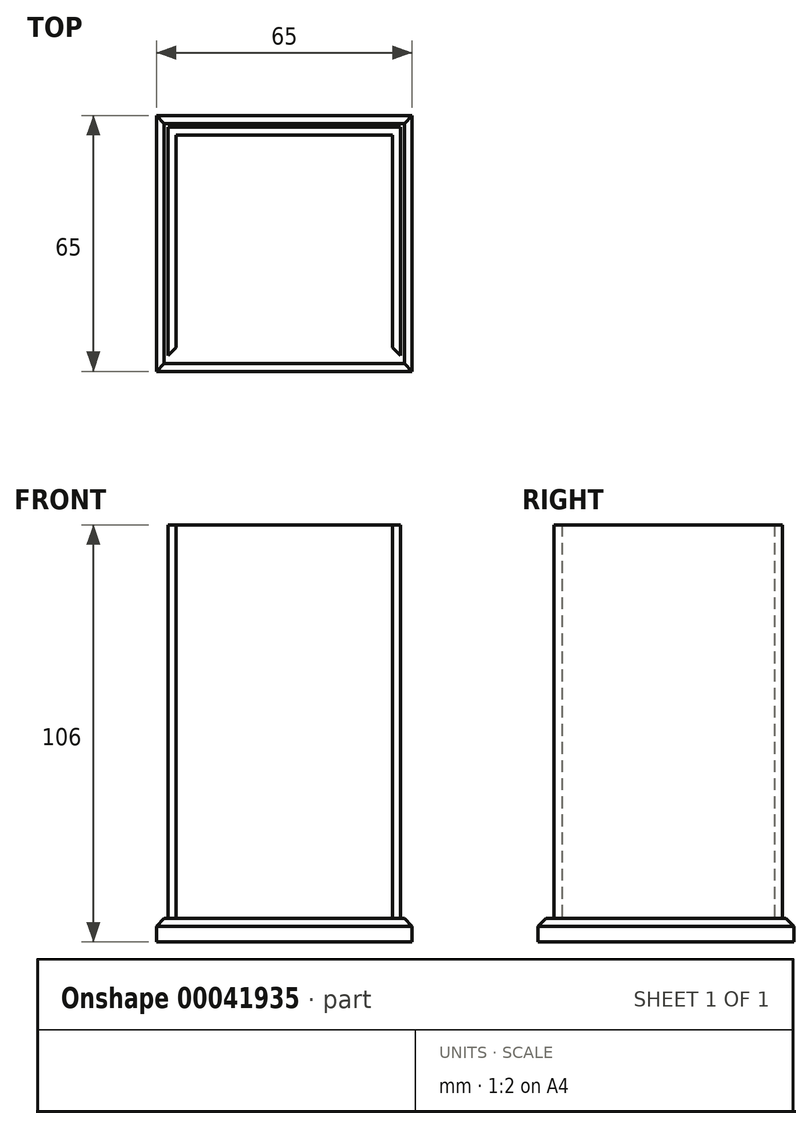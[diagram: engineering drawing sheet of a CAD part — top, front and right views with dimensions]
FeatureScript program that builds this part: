
annotation { "Feature Type Name" : "Feature", "Feature Type Description" : "" }
export const myFeature = defineFeature(function(context is Context, id is Id, definition is map)
    precondition{}
    {
        {
            var Q0;
            Q0=qCreatedBy(makeId("Top.planeOp"),FACE);
            var sketch = newSketch(context, id + "F0", { "sketchPlane" : qUnion([Q0])});
            skLineSegment(sketch, "E0.rect.bottom", {"start": v(32.5, -32.5) * mm, "end": v(-32.5, -32.5) * mm});
            skLineSegment(sketch, "E0.rect.top", {"start": v(32.5, 32.5) * mm, "end": v(-32.5, 32.5) * mm});
            skLineSegment(sketch, "E0.rect.left", {"start": v(32.5, -32.5) * mm, "end": v(32.5, 32.5) * mm});
            skLineSegment(sketch, "E0.rect.right", {"start": v(-32.5, -32.5) * mm, "end": v(-32.5, 32.5) * mm});
            skPoint(sketch, "E0.rect.middle", {"position": v(0, 0) * mm});
            skSolve(sketch);
        }
        {
            var Q0;
            Q0 = qSketchRegion(id + "F0", true);
            extrude(context, id + "F1", {"entities" : qUnion([Q0]), "depth" : 6 * mm});
        }
        {
            var Q0;
            Q0=makeQuery(id+"F1.opExtrude","CAP_FACE",FACE,{"disambiguationData":[OSD([sQuery(id+"F0.wireOp",EDGE,"E0.rect.bottom"),sQuery(id+"F0.wireOp",EDGE,"E0.rect.top"),sQuery(id+"F0.wireOp",EDGE,"E0.rect.left"),sQuery(id+"F0.wireOp",EDGE,"E0.rect.right")])],"isStart":false});
            chamfer(context, id + "F2", {"entities" : qUnion([Q0]), "width" : 2 * mm, "tangentPropagation" : true});
        }
        {
            var Q0;
            Q0=makeQuery(id+"F1.opExtrude","CAP_FACE",FACE,{"disambiguationData":[OSD([sQuery(id+"F0.wireOp",EDGE,"E0.rect.bottom"),sQuery(id+"F0.wireOp",EDGE,"E0.rect.top"),sQuery(id+"F0.wireOp",EDGE,"E0.rect.left"),sQuery(id+"F0.wireOp",EDGE,"E0.rect.right")])],"isStart":false});
            var sketch = newSketch(context, id + "F3", { "sketchPlane" : qUnion([Q0])});
            skLineSegment(sketch, "E1.0", {"start": v(29.5, -28.5) * mm, "end": v(29.5, 29.5) * mm});
            skLineSegment(sketch, "E1.2", {"start": v(-29.5, 29.5) * mm, "end": v(-29.5, -28.5) * mm});
            skLineSegment(sketch, "E1.3", {"start": v(29.5, 29.5) * mm, "end": v(-29.5, 29.5) * mm});
            skLineSegment(sketch, "E2.0", {"start": v(27.5, -26.5) * mm, "end": v(27.5, 27.5) * mm});
            skLineSegment(sketch, "E2.2", {"start": v(-27.5, 27.5) * mm, "end": v(-27.5, -26.5) * mm});
            skLineSegment(sketch, "E2.3", {"start": v(27.5, 27.5) * mm, "end": v(-27.5, 27.5) * mm});
            skLineSegment(sketch, "E3", {"start": v(-29.5, -28.5) * mm, "end": v(-27.5, -26.5) * mm});
            skLineSegment(sketch, "E4", {"start": v(29.5, -28.5) * mm, "end": v(27.5, -26.5) * mm});
            skSolve(sketch);
        }
        {
            var Q0;
            Q0 = qSketchRegion(id + "F3", true);
            extrude(context, id + "F4", {"entities" : qUnion([Q0]), "operationType" : NewBodyOperationType.ADD, "depth" : 100 * mm});
        }
    });
